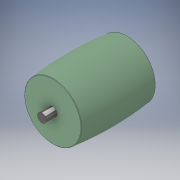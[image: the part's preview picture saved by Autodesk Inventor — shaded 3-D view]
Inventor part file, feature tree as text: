
AUTODESK INVENTOR PART (.ipt)
format: ipt  version: 2018 (Build 220112000, 112)  size: 220,672 bytes
history: native  units: in
note: dims shown in document units (in); Inventor stores cm internally (conversion verified against a paired STEP export)
features: sketch x7, plane x3, extrude x3, loft x1, fillet x1, mirror x1
ambient origin geometry x8: Origin, YZ Plane, XZ Plane, XY Plane, X Axis, Y Axis, Z Axis, Center Point
bodies: Solid1 (feature_tree)
feature tree (16):
  sketch  "Sketch1"  dims[d0=0.3346in d1=0.3346in d2=0.5118in]
  plane  "Work Plane3"
  loft  "Loft1"
  fillet  "Fillet1"  Radius=0.5118in
  extrude  "Extrusion1"  Depth=0.5118in
  mirror  "Mirror1"
  extrude  "Extrusion2"  TaperAngle=0.0deg  [1 undecoded]
  extrude  "Extrusion3"  Depth=0.0039in
  plane  "Work Plane1"
  plane  "Work Plane2"
  sketch  "Sketch2"  dims[d3=0.5512in d4=0.5118in]
  sketch  "Sketch3"  dims[d5=0.0in d6=90.0deg d7=0.0in d8=90.0deg]
  sketch  "Sketch4"  dims[d9=0.0in d10=90.0deg d11=0.0039in]
  sketch  "Sketch5"  dims[d12=0.0787in]
  sketch  "Sketch6"  dims[d13=0.1654in d14=0.0in]
  sketch  "Sketch7"  dims[d15=0.0669in d16=0.0in d17=0.0669in d18=0.0in]
note: 1 required parameter value undecoded (feature->parameter linkage not recoverable at this tier; creation-order binding heuristic only, values carry confidence <= 0.55)
